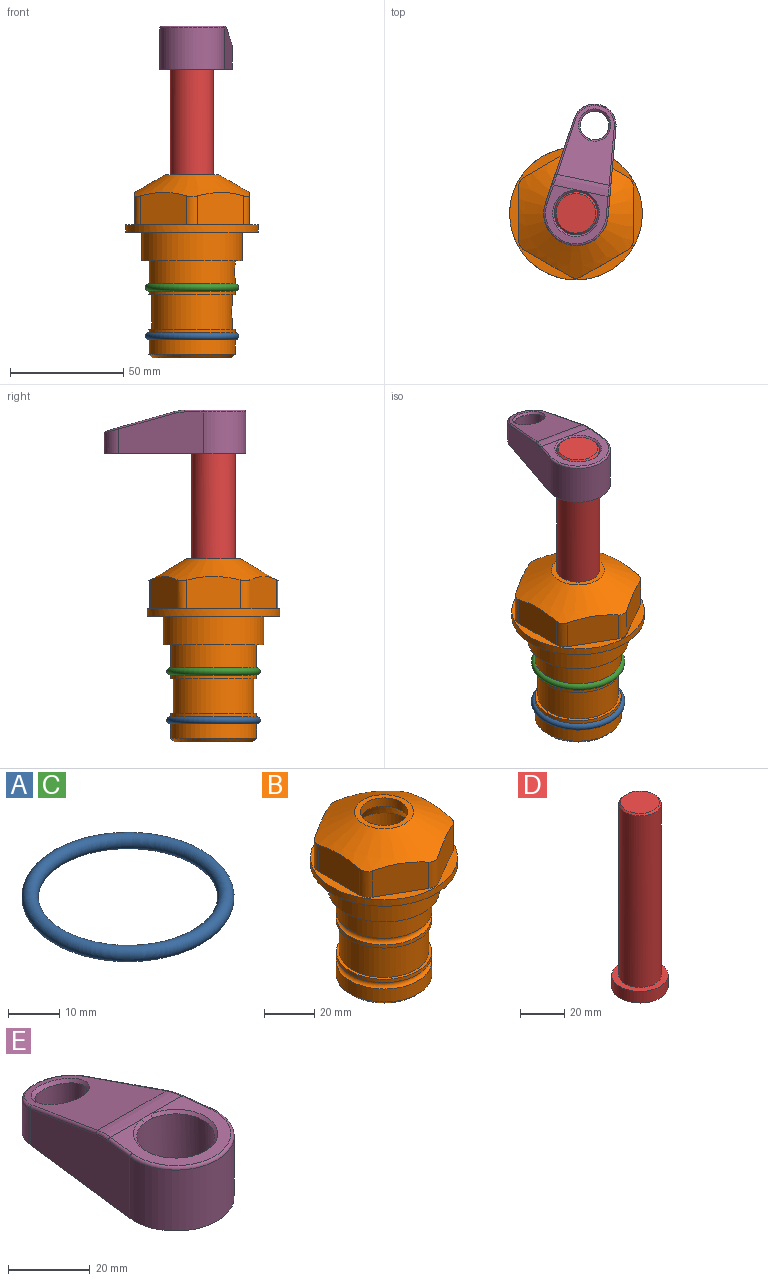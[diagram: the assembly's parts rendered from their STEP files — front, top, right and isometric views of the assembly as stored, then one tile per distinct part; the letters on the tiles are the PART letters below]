
ASSEMBLY  parts=5 mates=4
PART A: 1 faces, bbox 44.7x44.7x3.2 mm
  f0: torus R=19.05mm, axis (0,0,1), area 1193.9mm2
PART B: 36 faces, bbox 58.7x58.7x81 mm
  f0: cylinder r=17.78mm len=35.56mm, axis (0,0,1), area 1670.8mm2, adj f23,f24,f31
  f1: cylinder r=19.05mm len=38.1mm, axis (0,0,1), area 1191.9mm2, adj f26,f27,f30
  f2: plane 58.66x58.66mm, normal (0,0,-1), area 1150.6mm2, adj f3,f28
  f3: cylinder r=29.33mm len=58.66mm, axis (0,0,-1), area 585.1mm2, adj f2,f4
  f4: plane 58.66x58.66mm, normal (0,0,1), area 475.9mm2, adj f3,f5,f6,f7,f8,f9,f10,f11
  f5: plane 20.32x14.34mm, normal (-0.5,0.87,0), area 324.4mm2, adj f4,f15,f16,f17
  f6: plane 20.32x14.34mm, normal (0.5,0.87,0), area 324.4mm2, adj f4,f14,f15,f17
  f7: plane 23.48x14.34mm, normal (1,0,0), area 324.4mm2, adj f4,f13,f14,f17
  f8: plane 20.32x14.34mm, normal (0.5,-0.87,0), area 324.4mm2, adj f4,f12,f13,f17
  f9: plane 20.32x14.34mm, normal (-0.5,-0.87,0), area 324.4mm2, adj f4,f11,f12,f17
  f10: plane 23.48x14.34mm, normal (-1,0,0), area 324.4mm2, adj f4,f11,f16,f17
  f11: cylinder r=5.08mm len=12.85mm, axis (0,0,-1), area 67.2mm2, adj f4,f9,f10,f17
  f12: cylinder r=5.08mm len=12.85mm, axis (0,0,-1), area 67.2mm2, adj f4,f8,f9,f17
  f13: cylinder r=5.08mm len=12.85mm, axis (0,0,-1), area 67.2mm2, adj f4,f7,f8,f17
  f14: cylinder r=5.08mm len=12.85mm, axis (0,0,-1), area 67.2mm2, adj f4,f6,f7,f17
  f15: cylinder r=5.08mm len=12.85mm, axis (0,0,-1), area 67.2mm2, adj f4,f5,f6,f17
  f16: cylinder r=5.08mm len=12.85mm, axis (0,0,-1), area 67.2mm2, adj f4,f5,f10,f17
  f17: cone r=11.73mm half-angle=60deg, axis (0,0,-1), area 2071.8mm2, adj f5,f6,f7,f8,f9,f10,f11,f12
  f18: plane 23.46x23.46mm, normal (0,0,1), area 147.4mm2, adj f17,f35
  f19: plane 34.93x34.93mm, normal (0,0,-1), area 958mm2, adj f29
  f20: cylinder r=19.05mm len=38.1mm, axis (0,0,1), area 760.1mm2, adj f21,f29
  f21: torus R=19.05mm, axis (0,0,1), area 565.3mm2, adj f20,f22
  f22: cylinder r=19.05mm len=38.1mm, axis (0,0,1), area 190mm2, adj f21,f23
  f23: plane 38.1x38.1mm, normal (0,0,1), area 146.9mm2, adj f0,f22
  f24: plane 38.1x38.1mm, normal (0,0,-1), area 146.9mm2, adj f0,f25
  f25: cylinder r=19.05mm len=38.1mm, axis (0,0,1), area 190mm2, adj f24,f26
  f26: torus R=19.05mm, axis (0,0,1), area 565.3mm2, adj f1,f25
  f27: plane 44.45x44.45mm, normal (0,0,-1), area 411.7mm2, adj f1,f28
  f28: cylinder r=22.23mm len=44.45mm, axis (0,0,1), area 1773.5mm2, adj f2,f27
  f29: cone r=19.05mm half-angle=45deg, axis (0,0,1), area 257.5mm2, adj f19,f20
  f30: cylinder r=3.17mm len=6.75mm, axis (-1,0,0), area 128mm2, adj f1,f33
  f31: cylinder r=3.17mm len=6.35mm, axis (-1,0,0), area 102.5mm2, adj f0,f33
  f32: plane 25.4x25.4mm, normal (0,0,1), area 506.7mm2, adj f33
  f33: cylinder r=12.7mm len=66.42mm, axis (0,0,-1), area 5236.2mm2, adj f30,f31,f32,f34
  f34: cone r=9.53mm half-angle=30deg, axis (0,0,-1), area 443.4mm2, adj f33,f35
  f35: cylinder r=9.53mm len=19.05mm, axis (0,0,-1), area 240.9mm2, adj f18,f34
PART C: same geometry as A
PART D: 6 faces, bbox 25.4x25.4x101.6 mm
  f0: plane 17.46x17.46mm, normal (0,0,1), area 239.5mm2, adj f5
  f1: plane 25.4x25.4mm, normal (0,0,-1), area 506.7mm2, adj f2
  f2: cylinder r=12.7mm len=25.4mm, axis (0,0,1), area 506.7mm2, adj f1,f3
  f3: plane 25.4x25.4mm, normal (0,0,1), area 221.7mm2, adj f2,f4
  f4: cylinder r=9.53mm len=94.46mm, axis (0,0,1), area 5653mm2, adj f3,f5
  f5: cone r=8.73mm half-angle=45deg, axis (0,0,-1), area 64.4mm2, adj f0,f4
PART E: 31 faces, bbox 31.7x65.5x19.8 mm
  f0: plane 39.12x18.26mm, normal (0.99,0.12,0), area 612.2mm2, adj f1,f4,f7,f11,f13,f15
  f1: cylinder r=9.53mm len=18.91mm, axis (0,0,-1), area 296.1mm2, adj f0,f2,f7,f17
  f2: plane 39.12x18.26mm, normal (-0.99,0.12,0), area 612.2mm2, adj f1,f4,f7,f12,f14,f16
  f3: cylinder r=6.35mm len=12.7mm, axis (0,0,-1), area 362.4mm2, adj f7,f18
  f4: cylinder r=14.29mm len=28.58mm, axis (0,0,-1), area 882.2mm2, adj f0,f2,f7,f10
  f5: cylinder r=9.53mm len=19.05mm, axis (0,0,-1), area 1092.6mm2, adj f7,f19,f20
  f6: plane 26.99x23.69mm, normal (0,0,1), area 216.2mm2, adj f9,f10,f11,f12,f19
  f7: plane 63.5x28.58mm, normal (0,0,-1), area 661.8mm2, adj f0,f1,f2,f3,f4,f5,f22,f23
  f8: plane 33.52x23.6mm, normal (0,0.26,0.97), area 486mm2, adj f9,f15,f16,f17,f18
  f9: cylinder r=19.05mm len=24.72mm, axis (1,0,0), area 120.4mm2, adj f6,f8,f13,f14,f20
  f10: torus R=13.49mm, axis (0,0,1), area 59mm2, adj f4,f6,f11,f12
  f11: cylinder r=0.79mm len=8.67mm, axis (0.12,-0.99,0), area 10.8mm2, adj f0,f6,f10,f13
  f12: cylinder r=0.79mm len=8.67mm, axis (0.12,0.99,0), area 10.8mm2, adj f2,f6,f10,f14
  f13: bspline ~4.95x1.42mm, area 6.1mm2, adj f0,f9,f11,f15
  f14: bspline ~4.95x1.42mm, area 6.1mm2, adj f2,f9,f12,f16
  f15: cylinder r=0.79mm len=25.95mm, axis (0.12,-0.96,0.26), area 32.9mm2, adj f0,f8,f13,f17
  f16: cylinder r=0.79mm len=25.95mm, axis (0.12,0.96,-0.26), area 32.9mm2, adj f2,f8,f14,f17
  f17: bspline ~18.91x8.38mm, area 30mm2, adj f1,f8,f15,f16
  f18: bspline ~14.29x14.29mm, area 48.3mm2, adj f3,f8
  f19: cone r=9.53mm half-angle=45deg, axis (0,0,1), area 66.5mm2, adj f5,f6,f20
  f20: bspline ~3.22x0.96mm, area 3.5mm2, adj f5,f9,f19
  f21: plane 2.75x2.72mm, normal (0,0,-1), area 2.9mm2, adj f23,f25,f28
  f22: plane 23.05x15.88mm, normal (-0.99,-0.12,0), area 323.6mm2, adj f7,f25,f26,f27,f28,f29
  f23: plane 23.05x15.88mm, normal (0.99,-0.12,0), area 323.6mm2, adj f7,f21,f25,f27,f28,f30
  f24: cylinder r=9.53mm len=10.69mm, axis (0,0,-1), area 114.7mm2, adj f7,f27,f29,f30
  f25: cylinder r=12.7mm len=20.59mm, axis (0,0,-1), area 381.1mm2, adj f7,f21,f22,f23,f26,f28
  f26: plane 2.75x2.72mm, normal (0,0,-1), area 2.9mm2, adj f22,f25,f28
  f27: plane 19.72x18.37mm, normal (0,-0.26,-0.97), area 291.8mm2, adj f22,f23,f24,f28,f29,f30
  f28: cylinder r=15.88mm len=19.92mm, axis (1,0,0), area 54.8mm2, adj f21,f22,f23,f25,f26,f27
  f29: cylinder r=1.59mm len=11mm, axis (0,0,-1), area 34.7mm2, adj f7,f22,f24,f27
  f30: cylinder r=1.59mm len=11mm, axis (0,0,-1), area 34.7mm2, adj f7,f23,f24,f27
PLACE A t=(0,0,-21.59)mm
PLACE B at identity fixed
PLACE C at identity
PLACE D rot(axis=(0,0,-1),11.9deg) t=(0,0,27.55)mm
PLACE E rot(axis=(0,0,-1),11.9deg) t=(0,0,27.55)mm
MATE fastened A.f0 <-> B.f0  axis (0,0,1) through (0,0,-46.1)mm
MATE cylindrical D.f2 <-> B.f0  axis (0,0,-1) through (0,0,-10.55)mm
MATE fastened C.f0 <-> B.f0  axis (0,0,1) through (0,0,-24.51)mm
MATE fastened E.f4 <-> D.f2  axis (0,0,1) through (0,0,91.05)mm
